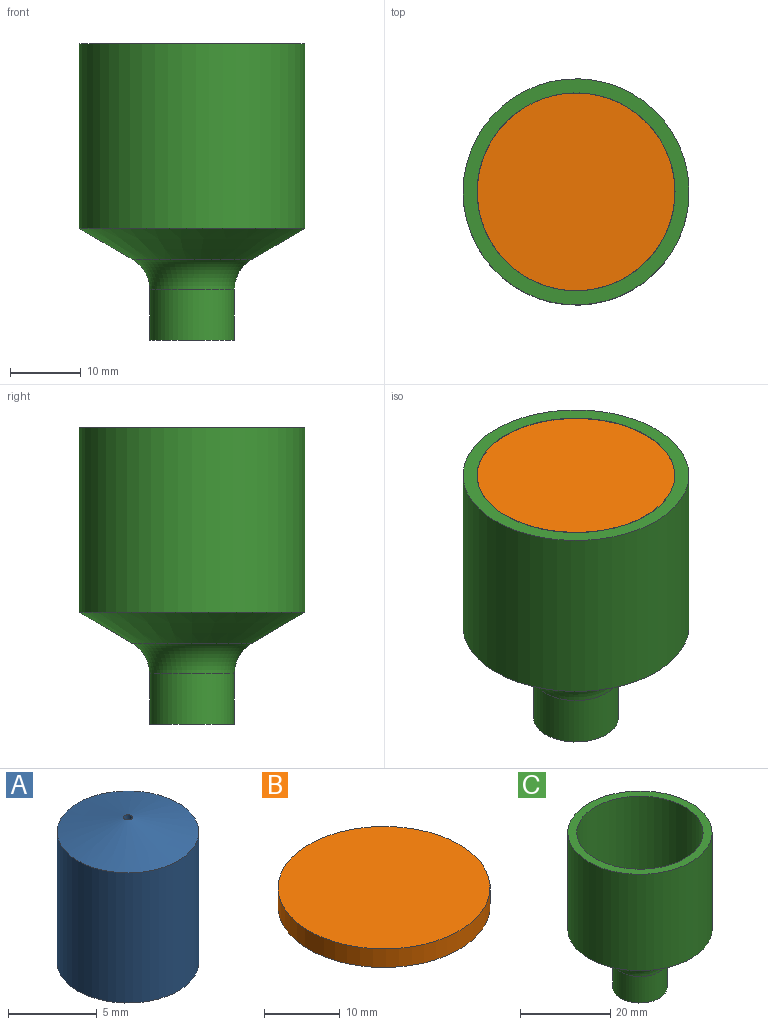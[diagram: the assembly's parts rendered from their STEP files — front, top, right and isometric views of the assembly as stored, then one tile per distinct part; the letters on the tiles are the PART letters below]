
ASSEMBLY  parts=3 mates=2
PART A: 7 faces, bbox 8x8x10 mm
  f0: plane 1.63x1.63mm, normal (0,0,-1), area 1.9mm2, adj f1,f6
  f1: cylinder r=0.25mm len=1mm, axis (0,0,-1), area 1.6mm2, adj f0,f2
  f2: cone r=0.25mm half-angle=75deg, axis (0,0,-1), area 51.8mm2, adj f1,f3
  f3: cylinder r=4mm len=8.99mm, axis (0,0,-1), area 226.1mm2, adj f2,f4
  f4: plane 8x8mm, normal (0,0,-1), area 22mm2, adj f3,f5
  f5: cylinder r=3mm len=8.41mm, axis (0,0,-1), area 158.6mm2, adj f4,f6
  f6: cone r=3mm half-angle=75deg, axis (0,0,-1), area 27.1mm2, adj f0,f5
PART B: 3 faces, bbox 28x28x3 mm
  f0: cylinder r=14mm len=28mm, axis (0,0,-1), area 263.9mm2, adj f1,f2
  f1: plane 28x28mm, normal (0,0,1), area 615.8mm2, adj f0
  f2: plane 28x28mm, normal (0,0,-1), area 615.8mm2, adj f0
PART C: 12 faces, bbox 32x32x42 mm
  f0: torus R=11mm, axis (0,0,-1), area 225.9mm2, adj f1,f11
  f1: cylinder r=6mm len=12mm, axis (0,0,-1), area 270.9mm2, adj f0,f2
  f2: plane 12x12mm, normal (0,0,-1), area 113.1mm2, adj f1
  f3: plane 4x4mm, normal (0,0,1), area 12.6mm2, adj f4
  f4: torus R=2mm, axis (0,0,-1), area 64.6mm2, adj f3,f5
  f5: cylinder r=4mm len=8mm, axis (0,0,-1), area 181.6mm2, adj f4,f6
  f6: cone r=11.5mm half-angle=60deg, axis (0,0,1), area 421.7mm2, adj f5,f7
  f7: torus R=9mm, axis (0,0,-1), area 432.1mm2, adj f6,f8
  f8: cylinder r=14mm len=28mm, axis (0,0,-1), area 1945.2mm2, adj f7,f9
  f9: plane 32x32mm, normal (0,0,1), area 188.5mm2, adj f8,f10
  f10: cylinder r=16mm len=32mm, axis (0,0,-1), area 2629.4mm2, adj f9,f11
  f11: cone r=16mm half-angle=60deg, axis (0,0,1), area 666.6mm2, adj f0,f10
PLACE A t=(-15.05,-0.64,-14.51)mm
PLACE B t=(-15.05,-0.64,17.99)mm
PLACE C t=(-15.05,-0.64,-20.96)mm fixed
MATE cylindrical B.f0 <-> C.f0  axis (0,0,-1) through (-15.05,-0.64,19.49)mm
MATE cylindrical A.f1 <-> C.f0  axis (0,0,-1) through (-15.05,-0.64,-10.01)mm
